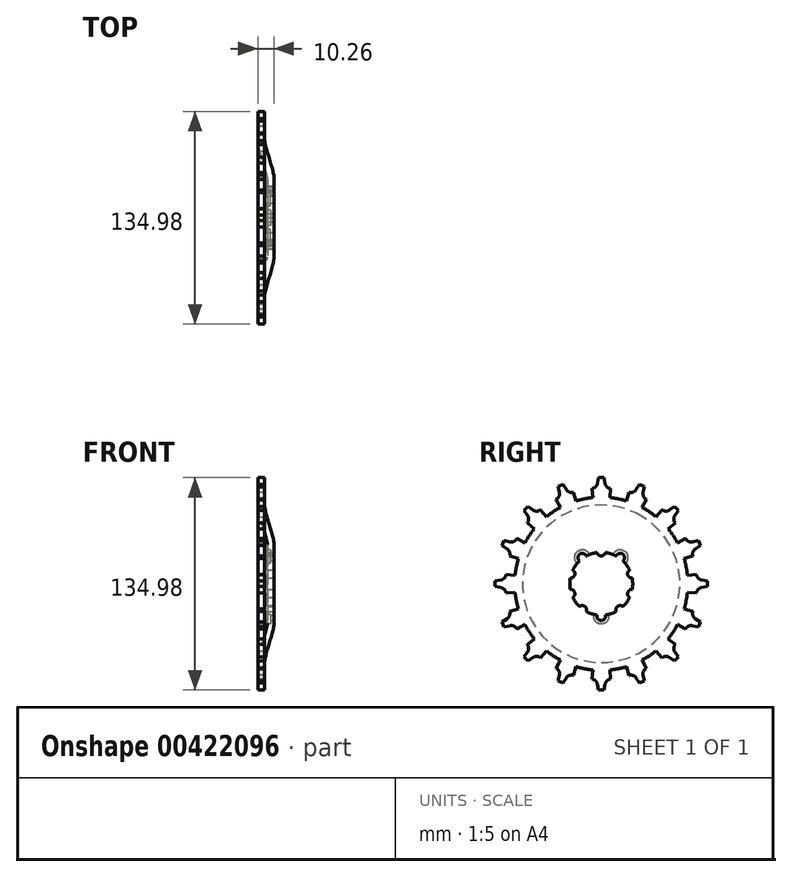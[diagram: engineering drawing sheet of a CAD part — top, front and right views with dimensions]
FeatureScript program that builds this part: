
annotation { "Feature Type Name" : "Feature", "Feature Type Description" : "" }
export const myFeature = defineFeature(function(context is Context, id is Id, definition is map)
    precondition{}
    {
        {
            var Q0;
            Q0=qCreatedBy(makeId("Right.planeOp"),FACE);
            var sketch = newSketch(context, id + "F0", { "sketchPlane" : qUnion([Q0])});
            skArc(sketch, "E0", {"start": v(5.96, 60.5) * mm, "mid": v(0, 60.78) * mm, "end": v(-5.96, 60.5) * mm, "construction": true});
            skLineSegment(sketch, "E1", {"start": v(0, 0) * mm, "end": v(-5.96, 60.5) * mm});
            skLineSegment(sketch, "E2", {"start": v(0, 0) * mm, "end": v(5.96, 60.5) * mm});
            skLineSegment(sketch, "E3", {"start": v(0, 0) * mm, "end": v(0, 64.43) * mm, "construction": true});
            skArc(sketch, "E4", {"start": v(-5.96, 60.5) * mm, "mid": v(-3.63, 61.54) * mm, "end": v(-2.41, 63.78) * mm});
            skLineSegment(sketch, "E5", {"start": v(-5.96, 60.5) * mm, "end": v(-10.86, 60) * mm, "construction": true});
            skArc(sketch, "E6.0.MirrorCS", {"start": v(5.96, 60.5) * mm, "mid": v(3.63, 61.54) * mm, "end": v(2.41, 63.78) * mm});
            skLineSegment(sketch, "E7", {"start": v(-2.41, 63.78) * mm, "end": v(-1.76, 67.5) * mm});
            skLineSegment(sketch, "E8", {"start": v(2.41, 63.78) * mm, "end": v(1.76, 67.5) * mm});
            skLineSegment(sketch, "E9", {"start": v(-1.76, 67.5) * mm, "end": v(1.76, 67.5) * mm});
            skSolve(sketch);
        }
        {
            var Q0;
            Q0=makeQuery(id+"F0.imprint","IMPRINT",FACE,{"disambiguationData":[TD([[makeQuery(id+"F0.imprint","IMPRINT",EDGE,{"derivedFrom":sQuery(id+"F0.wireOp",EDGE,"E1")}),-1.0]])]});
            extrude(context, id + "F1", {"entities" : qUnion([Q0]), "endBound" : BoundingType.SYMMETRIC, "depth" : 4.25 * mm});
        }
        {
            var Q0;
            Q0=qCreatedBy(makeId("Top.planeOp"),FACE);
            var sketch = newSketch(context, id + "F2", { "sketchPlane" : qUnion([Q0])});
            skLineSegment(sketch, "E10", {"start": v(0, 0) * mm, "end": v(43.96, 0) * mm});
            skSolve(sketch);
        }
        {
            var Q0;
            {var subQ0=makeQuery(id+"F1.opExtrude","CAP_FACE",FACE,{"disambiguationData":[OSD([sQuery(id+"F0.wireOp",EDGE,"E1"),sQuery(id+"F0.wireOp",EDGE,"E2"),sQuery(id+"F0.wireOp",EDGE,"E4"),sQuery(id+"F0.wireOp",EDGE,"E6.0.MirrorCS"),sQuery(id+"F0.wireOp",EDGE,"E7"),sQuery(id+"F0.wireOp",EDGE,"E8"),sQuery(id+"F0.wireOp",EDGE,"E9")])],"isStart":false});Q0=makeQuery(id+"F7VcO7OP56foUPZ_1.boolean.opBoolean","MERGE",FACE,{"derivedFrom":[subQ0,makeQuery(id+"F7VcO7OP56foUPZ_1.opPattern","COPY",FACE,{"derivedFrom":subQ0,"instanceName":"1"}),makeQuery(id+"F7VcO7OP56foUPZ_1.opPattern","COPY",FACE,{"derivedFrom":subQ0,"instanceName":"2"}),makeQuery(id+"F7VcO7OP56foUPZ_1.opPattern","COPY",FACE,{"derivedFrom":subQ0,"instanceName":"3"}),makeQuery(id+"F7VcO7OP56foUPZ_1.opPattern","COPY",FACE,{"derivedFrom":subQ0,"instanceName":"4"}),makeQuery(id+"F7VcO7OP56foUPZ_1.opPattern","COPY",FACE,{"derivedFrom":subQ0,"instanceName":"5"}),makeQuery(id+"F7VcO7OP56foUPZ_1.opPattern","COPY",FACE,{"derivedFrom":subQ0,"instanceName":"6"}),makeQuery(id+"F7VcO7OP56foUPZ_1.opPattern","COPY",FACE,{"derivedFrom":subQ0,"instanceName":"7"}),makeQuery(id+"F7VcO7OP56foUPZ_1.opPattern","COPY",FACE,{"derivedFrom":subQ0,"instanceName":"8"}),makeQuery(id+"F7VcO7OP56foUPZ_1.opPattern","COPY",FACE,{"derivedFrom":subQ0,"instanceName":"9"}),makeQuery(id+"F7VcO7OP56foUPZ_1.opPattern","COPY",FACE,{"derivedFrom":subQ0,"instanceName":"10"}),makeQuery(id+"F7VcO7OP56foUPZ_1.opPattern","COPY",FACE,{"derivedFrom":subQ0,"instanceName":"11"}),makeQuery(id+"F7VcO7OP56foUPZ_1.opPattern","COPY",FACE,{"derivedFrom":subQ0,"instanceName":"12"}),makeQuery(id+"F7VcO7OP56foUPZ_1.opPattern","COPY",FACE,{"derivedFrom":subQ0,"instanceName":"13"}),makeQuery(id+"F7VcO7OP56foUPZ_1.opPattern","COPY",FACE,{"derivedFrom":subQ0,"instanceName":"14"}),makeQuery(id+"F7VcO7OP56foUPZ_1.opPattern","COPY",FACE,{"derivedFrom":subQ0,"instanceName":"15"}),makeQuery(id+"F7VcO7OP56foUPZ_1.opPattern","COPY",FACE,{"derivedFrom":subQ0,"instanceName":"16"}),makeQuery(id+"F7VcO7OP56foUPZ_1.opPattern","COPY",FACE,{"derivedFrom":subQ0,"instanceName":"17"}),makeQuery(id+"F7VcO7OP56foUPZ_1.opPattern","COPY",FACE,{"derivedFrom":subQ0,"instanceName":"18"}),makeQuery(id+"F7VcO7OP56foUPZ_1.opPattern","COPY",FACE,{"derivedFrom":subQ0,"instanceName":"19"}),makeQuery(id+"F7VcO7OP56foUPZ_1.opPattern","COPY",FACE,{"derivedFrom":subQ0,"instanceName":"20"}),makeQuery(id+"F7VcO7OP56foUPZ_1.opPattern","COPY",FACE,{"derivedFrom":subQ0,"instanceName":"21"}),makeQuery(id+"F7VcO7OP56foUPZ_1.opPattern","COPY",FACE,{"derivedFrom":subQ0,"instanceName":"22"}),makeQuery(id+"F7VcO7OP56foUPZ_1.opPattern","COPY",FACE,{"derivedFrom":subQ0,"instanceName":"23"}),makeQuery(id+"F7VcO7OP56foUPZ_1.opPattern","COPY",FACE,{"derivedFrom":subQ0,"instanceName":"24"}),makeQuery(id+"F7VcO7OP56foUPZ_1.opPattern","COPY",FACE,{"derivedFrom":subQ0,"instanceName":"25"}),makeQuery(id+"F7VcO7OP56foUPZ_1.opPattern","COPY",FACE,{"derivedFrom":subQ0,"instanceName":"26"}),makeQuery(id+"F7VcO7OP56foUPZ_1.opPattern","COPY",FACE,{"derivedFrom":subQ0,"instanceName":"27"}),makeQuery(id+"F7VcO7OP56foUPZ_1.opPattern","COPY",FACE,{"derivedFrom":subQ0,"instanceName":"28"}),makeQuery(id+"F7VcO7OP56foUPZ_1.opPattern","COPY",FACE,{"derivedFrom":subQ0,"instanceName":"29"}),makeQuery(id+"F7VcO7OP56foUPZ_1.opPattern","COPY",FACE,{"derivedFrom":subQ0,"instanceName":"30"}),makeQuery(id+"F7VcO7OP56foUPZ_1.opPattern","COPY",FACE,{"derivedFrom":subQ0,"instanceName":"31"})]});}
            var sketch = newSketch(context, id + "F3", { "sketchPlane" : qUnion([Q0])});
            skCircle(sketch, "E11", {"center": v(0, 0) * mm, "radius": 55 * mm});
            skSolve(sketch);
        }
        {
            var Q0;
            Q0=makeQuery(id+"F3.imprint","IMPRINT",FACE,{"disambiguationData":[TD([[makeQuery(id+"F3.imprint","IMPRINT",EDGE,{"derivedFrom":sQuery(id+"F3.wireOp",EDGE,"E11")}),1.0]])]});
            extrude(context, id + "F4", {"entities" : qUnion([Q0]), "operationType" : NewBodyOperationType.REMOVE, "endBound" : BoundingType.THROUGH_ALL, "oppositeDirection" : true, "depth" : 25 * mm});
        }
        {
            var Q0;
            Q0=qCreatedBy(makeId("Front.planeOp"),FACE);
            var sketch = newSketch(context, id + "F5", { "sketchPlane" : qUnion([Q0])});
            skLineSegment(sketch, "E12", {"start": v(-2.12, 55) * mm, "end": v(2.13, 55) * mm});
            skLineSegment(sketch, "E13", {"start": v(8.13, 0) * mm, "end": v(8.13, 25) * mm});
            skLineSegment(sketch, "E14", {"start": v(2.13, 55) * mm, "end": v(2.13, 50) * mm});
            skFitSpline(sketch, "E15", {"points": [v(2.13, 50) * mm, v(8.13, 25) * mm], "startDerivative": vector(0, -15) * mm, "endDerivative": vector(0, -15) * mm});
            skLineSegment(sketch, "E16", {"start": v(-2.12, 55) * mm, "end": v(-2.12, 50) * mm});
            skLineSegment(sketch, "E17", {"start": v(8.13, 0) * mm, "end": v(3.88, 0) * mm});
            skLineSegment(sketch, "E18", {"start": v(3.88, 0) * mm, "end": v(3.88, 25) * mm});
            skFitSpline(sketch, "E19.0", {"points": [v(-2.12, 50) * mm, v(-2.12, 49.48) * mm, v(-2.05, 48.47) * mm, v(-1.81, 46.94) * mm, v(-1.48, 45.34) * mm, v(-0.93, 43.08) * mm, v(-0.08, 40.05) * mm, v(1.06, 36.27) * mm, v(2.17, 32.55) * mm, v(2.96, 29.72) * mm, v(3.44, 27.76) * mm, v(3.7, 26.5) * mm, v(3.85, 25.5) * mm, v(3.87, 25.1) * mm, v(3.87, 25) * mm]});
            skSolve(sketch);
        }
        {
            var Q0;
            Q0=makeQuery(id+"F5.imprint","IMPRINT",FACE,{"disambiguationData":[TD([[makeQuery(id+"F5.imprint","IMPRINT",EDGE,{"derivedFrom":sQuery(id+"F5.wireOp",EDGE,"E12")}),-1.0]])]});
            var Q1;
            Q1=sQuery(id+"F2.wireOp",EDGE,"E10");
            revolve(context, id + "F6", {"operationType" : NewBodyOperationType.ADD, "entities" : qUnion([Q0]), "axis" : qUnion([Q1]), "revolveType" : RevolveType.TWO_DIRECTIONS, "oppositeDirection" : true, "angle" : 16.88 * degree, "angleBack" : 360 * degree - ((360 / 64) * degree)});
        }
        {
            var Q0;
            Q0=makeQuery(id+"F6.opRevolve","SWEPT_FACE",FACE,{"disambiguationData":[OSD([sQuery(id+"F5.wireOp",EDGE,"E13")])]});
            var sketch = newSketch(context, id + "F7", { "sketchPlane" : qUnion([Q0])});
            skCircle(sketch, "E20", {"center": v(0, 0) * mm, "radius": 20 * mm});
            skSolve(sketch);
        }
        {
            var Q0;
            Q0=makeQuery(id+"F7.imprint","IMPRINT",FACE,{"disambiguationData":[TD([[makeQuery(id+"F7.imprint","IMPRINT",EDGE,{"derivedFrom":sQuery(id+"F7.wireOp",EDGE,"E20")}),1.0]])]});
            var Q1;
            Q1=sQuery(id+"F7.wireOp",EDGE,"E20");
            extrude(context, id + "F8", {"entities" : qUnion([Q0]), "operationType" : NewBodyOperationType.REMOVE, "surfaceEntities" : qUnion([Q1]), "endBound" : BoundingType.THROUGH_ALL, "oppositeDirection" : true, "depth" : 25 * mm});
        }
        {
            var Q0;
            Q0=makeQuery(id+"F1.opExtrude","SWEPT_BODY",BODY,{"disambiguationData":[OSD([sQuery(id+"F0.wireOp",EDGE,"E1"),sQuery(id+"F0.wireOp",EDGE,"E2"),sQuery(id+"F0.wireOp",EDGE,"E4"),sQuery(id+"F0.wireOp",EDGE,"E6.0.MirrorCS"),sQuery(id+"F0.wireOp",EDGE,"E7"),sQuery(id+"F0.wireOp",EDGE,"E8"),sQuery(id+"F0.wireOp",EDGE,"E9")])]});
            var Q1;
            Q1=sQuery(id+"F2.wireOp",EDGE,"E10");
            circularPattern(context, id + "F9", {"operationType" : NewBodyOperationType.ADD, "entities" : qUnion([Q0]), "axis" : qUnion([Q1]), "angle" : 360 * degree, "instanceCount" : 16, "equalSpace" : true});
        }
        {
            var Q0;
            Q0=makeQuery(id+"F6.opRevolve","SWEPT_FACE",FACE,{"disambiguationData":[OSD([sQuery(id+"F5.wireOp",EDGE,"E13")])]});
            var sketch = newSketch(context, id + "F10", { "sketchPlane" : qUnion([Q0])});
            skCircle(sketch, "E21", {"center": v(0, -20.5) * mm, "radius": 2.75 * mm});
            skCircle(sketch, "E22.0", {"center": v(0, 0) * mm, "radius": 20.5 * mm, "construction": true});
            skSolve(sketch);
        }
        {
            var Q0;
            Q0=qSketchRegion(id+"F10",true);
            var Q1;
            Q1=makeQuery(id+"F6.opRevolve","SWEPT_FACE",FACE,{"disambiguationData":[OSD([sQuery(id+"F5.wireOp",EDGE,"E18")])]});
            extrude(context, id + "F11", {"entities" : qUnion([Q0]), "operationType" : NewBodyOperationType.ADD, "endBound" : BoundingType.UP_TO_SURFACE, "oppositeDirection" : true, "endBoundEntityFace" : qUnion([Q1]), "depth" : 25 * mm});
        }
        {
            var Q0;
            Q0=makeQuery(id+"F11.opExtrude","SWEPT_FACE",FACE,{"disambiguationData":[OSD([sQuery(id+"F10.wireOp",EDGE,"E21")])]});
            var Q1;
            Q1=sQuery(id+"F2.wireOp",EDGE,"E10");
            circularPattern(context, id + "F12", {"faces" : qUnion([Q0]), "axis" : qUnion([Q1]), "angle" : 360 * degree, "instanceCount" : 10, "equalSpace" : true, "patternType" : PatternType.FACE});
        }
        {
            var Q0;
            {var subQ0=makeQuery(id+"F6.opRevolve","SWEPT_FACE",FACE,{"disambiguationData":[OSD([sQuery(id+"F5.wireOp",EDGE,"E13")])]});Q0=makeQuery(id+"F11.boolean.opBoolean","MERGE",FACE,{"derivedFrom":[makeQuery(id+"F9.boolean.opBoolean","MERGE",FACE,{"derivedFrom":[subQ0,makeQuery(id+"F9.opPattern","COPY",FACE,{"derivedFrom":subQ0,"instanceName":"1"}),makeQuery(id+"F9.opPattern","COPY",FACE,{"derivedFrom":subQ0,"instanceName":"2"}),makeQuery(id+"F9.opPattern","COPY",FACE,{"derivedFrom":subQ0,"instanceName":"3"}),makeQuery(id+"F9.opPattern","COPY",FACE,{"derivedFrom":subQ0,"instanceName":"4"}),makeQuery(id+"F9.opPattern","COPY",FACE,{"derivedFrom":subQ0,"instanceName":"5"}),makeQuery(id+"F9.opPattern","COPY",FACE,{"derivedFrom":subQ0,"instanceName":"6"}),makeQuery(id+"F9.opPattern","COPY",FACE,{"derivedFrom":subQ0,"instanceName":"7"}),makeQuery(id+"F9.opPattern","COPY",FACE,{"derivedFrom":subQ0,"instanceName":"8"}),makeQuery(id+"F9.opPattern","COPY",FACE,{"derivedFrom":subQ0,"instanceName":"9"}),makeQuery(id+"F9.opPattern","COPY",FACE,{"derivedFrom":subQ0,"instanceName":"10"}),makeQuery(id+"F9.opPattern","COPY",FACE,{"derivedFrom":subQ0,"instanceName":"11"}),makeQuery(id+"F9.opPattern","COPY",FACE,{"derivedFrom":subQ0,"instanceName":"12"}),makeQuery(id+"F9.opPattern","COPY",FACE,{"derivedFrom":subQ0,"instanceName":"13"}),makeQuery(id+"F9.opPattern","COPY",FACE,{"derivedFrom":subQ0,"instanceName":"14"}),makeQuery(id+"F9.opPattern","COPY",FACE,{"derivedFrom":subQ0,"instanceName":"15"})]}),makeQuery(id+"F11.opExtrude","CAP_FACE",FACE,{"disambiguationData":[OSD([sQuery(id+"F10.wireOp",EDGE,"E21")])],"isStart":true})]});}
            var sketch = newSketch(context, id + "F13", { "sketchPlane" : qUnion([Q0])});
            skCircle(sketch, "E23", {"center": v(0, -20.5) * mm, "radius": 2.75 * mm});
            skCircle(sketch, "E24", {"center": v(-12.05, 16.58) * mm, "radius": 2.75 * mm});
            skCircle(sketch, "E25", {"center": v(12.05, 16.58) * mm, "radius": 2.75 * mm});
            skSolve(sketch);
        }
        {
            var Q0;
            Q0=qSketchRegion(id+"F13",true);
            extrude(context, id + "F14", {"entities" : qUnion([Q0]), "operationType" : NewBodyOperationType.REMOVE, "endBound" : BoundingType.THROUGH_ALL, "oppositeDirection" : true, "depth" : 25 * mm});
        }
        {
            var Q0;
            {var subQ0=sQuery(id+"F5.wireOp",EDGE,"E18");var subQ1=makeQuery(id+"F6.opRevolve","SWEPT_FACE",FACE,{"disambiguationData":[OSD([subQ0])]});Q0=makeQuery(id+"F11.boolean.opBoolean","MERGE",FACE,{"derivedFrom":[makeQuery(id+"F9.boolean.opBoolean","MERGE",FACE,{"derivedFrom":[subQ1,makeQuery(id+"F9.opPattern","COPY",FACE,{"derivedFrom":subQ1,"instanceName":"1"}),makeQuery(id+"F9.opPattern","COPY",FACE,{"derivedFrom":subQ1,"instanceName":"2"}),makeQuery(id+"F9.opPattern","COPY",FACE,{"derivedFrom":subQ1,"instanceName":"3"}),makeQuery(id+"F9.opPattern","COPY",FACE,{"derivedFrom":subQ1,"instanceName":"4"}),makeQuery(id+"F9.opPattern","COPY",FACE,{"derivedFrom":subQ1,"instanceName":"5"}),makeQuery(id+"F9.opPattern","COPY",FACE,{"derivedFrom":subQ1,"instanceName":"6"}),makeQuery(id+"F9.opPattern","COPY",FACE,{"derivedFrom":subQ1,"instanceName":"7"}),makeQuery(id+"F9.opPattern","COPY",FACE,{"derivedFrom":subQ1,"instanceName":"8"}),makeQuery(id+"F9.opPattern","COPY",FACE,{"derivedFrom":subQ1,"instanceName":"9"}),makeQuery(id+"F9.opPattern","COPY",FACE,{"derivedFrom":subQ1,"instanceName":"10"}),makeQuery(id+"F9.opPattern","COPY",FACE,{"derivedFrom":subQ1,"instanceName":"11"}),makeQuery(id+"F9.opPattern","COPY",FACE,{"derivedFrom":subQ1,"instanceName":"12"}),makeQuery(id+"F9.opPattern","COPY",FACE,{"derivedFrom":subQ1,"instanceName":"13"}),makeQuery(id+"F9.opPattern","COPY",FACE,{"derivedFrom":subQ1,"instanceName":"14"}),makeQuery(id+"F9.opPattern","COPY",FACE,{"derivedFrom":subQ1,"instanceName":"15"})]}),makeQuery(id+"F11.opExtrude","CAP_FACE",FACE,{"disambiguationData":[OSD([subQ0])],"isStart":false})]});}
            var sketch = newSketch(context, id + "F15", { "sketchPlane" : qUnion([Q0])});
            skCircle(sketch, "E26", {"center": v(-12.05, 16.58) * mm, "radius": 5 * mm});
            skCircle(sketch, "E27", {"center": v(12.05, 16.58) * mm, "radius": 5 * mm});
            skCircle(sketch, "E28", {"center": v(0, -20.5) * mm, "radius": 5 * mm});
            skSolve(sketch);
        }
        {
            var Q0;
            Q0=qSketchRegion(id+"F15",true);
            extrude(context, id + "F16", {"entities" : qUnion([Q0]), "operationType" : NewBodyOperationType.REMOVE, "oppositeDirection" : true, "depth" : 2 * mm, "hasSecondDirection" : true, "secondDirectionBound" : SecondDirectionBoundingType.THROUGH_ALL, "secondDirectionOppositeDirection" : false, "secondDirectionDepth" : 25 * mm});
        }
    });
